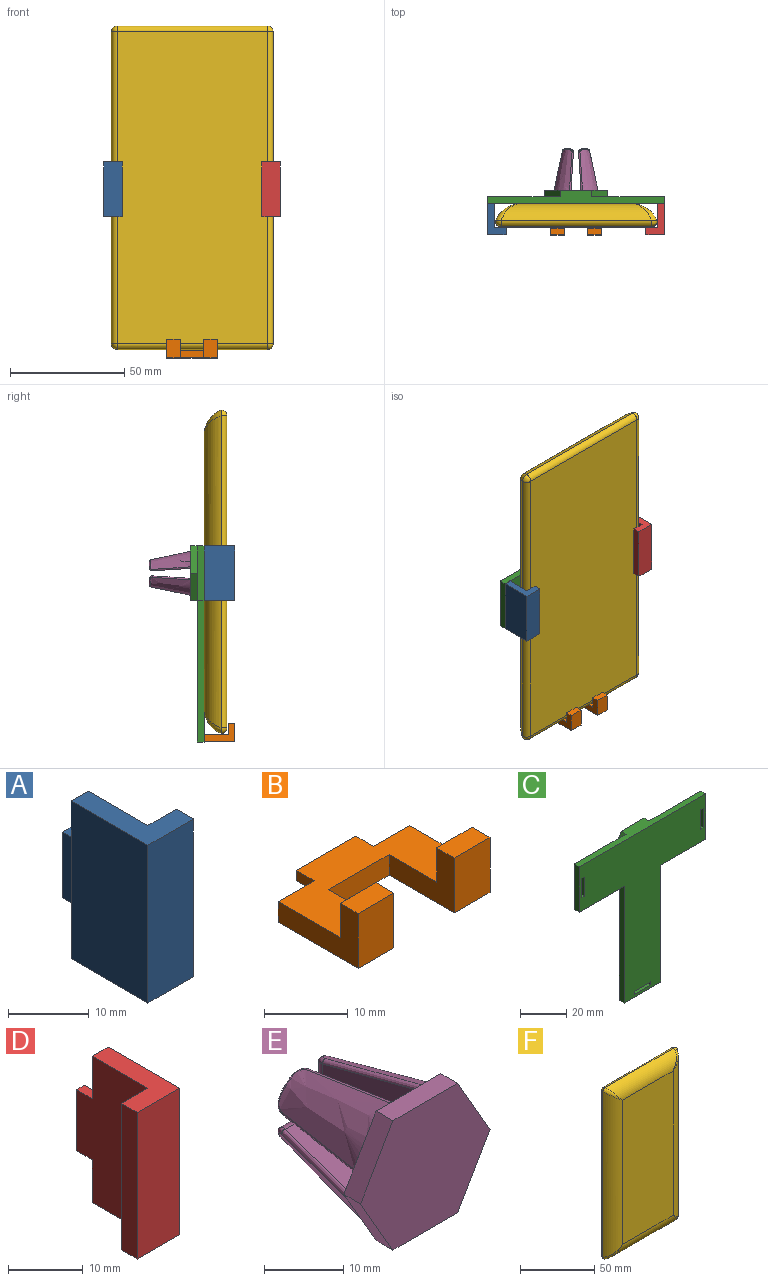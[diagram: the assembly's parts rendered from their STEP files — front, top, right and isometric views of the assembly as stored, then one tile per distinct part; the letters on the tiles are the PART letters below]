
ASSEMBLY  parts=6 mates=5
PART A: 12 faces, bbox 8x16.5x24 mm
  f0: plane 13.5x8mm, normal (0,0,-1), area 55.5mm2, adj f1,f4,f5,f6,f7,f11
  f1: plane 24x13.5mm, normal (1,0,0), area 282mm2, adj f0,f2,f3,f7,f8,f10,f11
  f2: plane 13.5x8mm, normal (0,0,1), area 55.5mm2, adj f1,f4,f5,f6,f7,f11
  f3: plane 10x1.5mm, normal (0,1,0), area 15mm2, adj f1,f8,f9,f10
  f4: plane 24x13.5mm, normal (-1,0,0), area 324mm2, adj f0,f2,f6,f11
  f5: plane 24x3mm, normal (1,0,0), area 72mm2, adj f0,f2,f6,f7
  f6: plane 24x8mm, normal (0,-1,0), area 192mm2, adj f0,f2,f4,f5
  f7: plane 24x5mm, normal (0,1,0), area 120mm2, adj f0,f1,f2,f5
  f8: plane 3x1.5mm, normal (0,0,1), area 4.5mm2, adj f1,f3,f9,f11
  f9: plane 10x3mm, normal (-1,0,0), area 30mm2, adj f3,f8,f10,f11
  f10: plane 3x1.5mm, normal (0,0,-1), area 4.5mm2, adj f1,f3,f9,f11
  f11: plane 24x3mm, normal (0,1,0), area 57mm2, adj f0,f1,f2,f4,f8,f9,f10
PART B: 18 faces, bbox 22.2x16.5x8 mm
  f0: plane 10x1.5mm, normal (0,1,0), area 15mm2, adj f1,f2,f3,f4
  f1: plane 22.2x13.5mm, normal (0,0,1), area 181.5mm2, adj f0,f3,f4,f5,f6,f7,f9,f12
  f2: plane 10x3mm, normal (0,0,-1), area 30mm2, adj f0,f3,f4,f5
  f3: plane 3x1.5mm, normal (-1,0,0), area 4.5mm2, adj f0,f1,f2,f5
  f4: plane 3x1.5mm, normal (1,0,0), area 4.5mm2, adj f0,f1,f2,f5
  f5: plane 22.2x3mm, normal (0,1,0), area 51.6mm2, adj f1,f2,f3,f4,f7,f8,f16
  f6: plane 11x8mm, normal (1,0,0), area 48mm2, adj f1,f8,f9,f10,f11,f17
  f7: plane 13.5x8mm, normal (-1,0,0), area 55.5mm2, adj f1,f5,f8,f9,f10,f11
  f8: plane 22.2x13.5mm, normal (0,0,-1), area 187.5mm2, adj f5,f6,f7,f11,f12,f15,f16,f17
  f9: plane 6x5mm, normal (0,1,0), area 30mm2, adj f1,f6,f7,f10
  f10: plane 6x3mm, normal (0,0,1), area 18mm2, adj f6,f7,f9,f11
  f11: plane 8x6mm, normal (0,-1,0), area 48mm2, adj f6,f7,f8,f10
  f12: plane 11x8mm, normal (-1,0,0), area 48mm2, adj f1,f8,f13,f14,f15,f17
  f13: plane 6x5mm, normal (0,1,0), area 30mm2, adj f1,f12,f14,f16
  f14: plane 6x3mm, normal (0,0,1), area 18mm2, adj f12,f13,f15,f16
  f15: plane 8x6mm, normal (0,-1,0), area 48mm2, adj f8,f12,f14,f16
  f16: plane 13.5x8mm, normal (1,0,0), area 55.5mm2, adj f1,f5,f8,f13,f14,f15
  f17: plane 10.2x3mm, normal (0,-1,0), area 30.6mm2, adj f1,f6,f8,f12
PART C: 35 faces, bbox 77.2x6x85.8 mm
  f0: plane 61.75x3mm, normal (-1,0,0), area 185.2mm2, adj f2,f3,f4,f5
  f1: plane 61.75x3mm, normal (1,0,0), area 185.2mm2, adj f2,f3,f4,f9
  f2: plane 22.2x3mm, normal (0,0,-1), area 66.6mm2, adj f0,f1,f3,f4
  f3: plane 85.75x77.2mm, normal (0,1,0), area 2676.3mm2, adj f0,f1,f2,f5,f6,f7,f8,f9
  f4: plane 85.75x77.2mm, normal (0,-1,0), area 3175.2mm2, adj f0,f1,f2,f5,f6,f7,f8,f9
  f5: plane 27.5x3mm, normal (0,0,-1), area 82.5mm2, adj f0,f3,f4,f8
  f6: plane 24x3mm, normal (1,0,0), area 72mm2, adj f3,f4,f7,f9
  f7: plane 77.2x6mm, normal (0,0,1), area 273.2mm2, adj f3,f4,f6,f8,f16,f17,f21
  f8: plane 24x3mm, normal (-1,0,0), area 72mm2, adj f3,f4,f5,f7
  f9: plane 27.5x3mm, normal (0,0,-1), area 82.5mm2, adj f1,f3,f4,f6
  f10: plane 10.1x5.83mm, normal (0.87,0,-0.5), area 35mm2, adj f11,f20,f21,f22
  f11: plane 10.1x5.83mm, normal (0.87,0,0.5), area 35mm2, adj f10,f12,f21,f22
  f12: plane 11.66x3mm, normal (0,0,1), area 35mm2, adj f11,f13,f21,f22
  f13: plane 10.1x5.83mm, normal (-0.87,0,0.5), area 35mm2, adj f12,f14,f21,f22
  f14: plane 10.1x5.83mm, normal (-0.87,0,-0.5), area 35mm2, adj f13,f20,f21,f22
  f15: plane 12x6.93mm, normal (-0.87,0,-0.5), area 41.6mm2, adj f3,f16,f19,f21
  f16: plane 12x6.93mm, normal (-0.87,0,0.5), area 41.6mm2, adj f3,f7,f15,f21
  f17: plane 12x6.93mm, normal (0.87,0,0.5), area 41.6mm2, adj f3,f7,f18,f21
  f18: plane 12x6.93mm, normal (0.87,0,-0.5), area 41.6mm2, adj f3,f17,f19,f21
  f19: plane 13.86x3mm, normal (0,0,-1), area 41.6mm2, adj f3,f15,f18,f21
  f20: plane 11.66x3mm, normal (0,0,-1), area 35mm2, adj f10,f14,f21,f22
  f21: plane 27.71x24mm, normal (0,1,0), area 145.5mm2, adj f7,f10,f11,f12,f13,f14,f15,f16
  f22: plane 23.33x20.2mm, normal (0,1,0), area 353.4mm2, adj f10,f11,f12,f13,f14,f20
  f23: plane 10.1x3mm, normal (1,0,0), area 30.3mm2, adj f3,f4,f24,f25
  f24: plane 3x1.6mm, normal (0,0,-1), area 4.8mm2, adj f3,f4,f23,f26
  f25: plane 3x1.6mm, normal (0,0,1), area 4.8mm2, adj f3,f4,f23,f26
  f26: plane 10.1x3mm, normal (-1,0,0), area 30.3mm2, adj f3,f4,f24,f25
  f27: plane 10.1x3mm, normal (0,0,1), area 30.3mm2, adj f3,f4,f28,f29
  f28: plane 3x1.6mm, normal (1,0,0), area 4.8mm2, adj f3,f4,f27,f30
  f29: plane 3x1.6mm, normal (-1,0,0), area 4.8mm2, adj f3,f4,f27,f30
  f30: plane 10.1x3mm, normal (0,0,-1), area 30.3mm2, adj f3,f4,f28,f29
  f31: plane 10.1x3mm, normal (1,0,0), area 30.3mm2, adj f3,f4,f32,f33
  f32: plane 3x1.6mm, normal (0,0,-1), area 4.8mm2, adj f3,f4,f31,f34
  f33: plane 3x1.6mm, normal (0,0,1), area 4.8mm2, adj f3,f4,f31,f34
  f34: plane 10.1x3mm, normal (-1,0,0), area 30.3mm2, adj f3,f4,f32,f33
PART D: 12 faces, bbox 8x16.5x24 mm
  f0: plane 13.5x8mm, normal (0,0,-1), area 55.5mm2, adj f1,f3,f5,f6,f7,f11
  f1: plane 24x13.5mm, normal (1,0,0), area 324mm2, adj f0,f4,f6,f11
  f2: plane 10x1.5mm, normal (0,1,0), area 15mm2, adj f3,f8,f9,f10
  f3: plane 24x13.5mm, normal (-1,0,0), area 282mm2, adj f0,f2,f4,f7,f8,f10,f11
  f4: plane 13.5x8mm, normal (0,0,1), area 55.5mm2, adj f1,f3,f5,f6,f7,f11
  f5: plane 24x3mm, normal (-1,0,0), area 72mm2, adj f0,f4,f6,f7
  f6: plane 24x8mm, normal (0,-1,0), area 192mm2, adj f0,f1,f4,f5
  f7: plane 24x5mm, normal (0,1,0), area 120mm2, adj f0,f3,f4,f5
  f8: plane 3x1.5mm, normal (0,0,-1), area 4.5mm2, adj f2,f3,f9,f11
  f9: plane 10x3mm, normal (1,0,0), area 30mm2, adj f2,f8,f10,f11
  f10: plane 3x1.5mm, normal (0,0,1), area 4.5mm2, adj f2,f3,f9,f11
  f11: plane 24x3mm, normal (0,1,0), area 57mm2, adj f0,f1,f3,f4,f8,f9,f10
PART E: 60 faces, bbox 23.2x23.4x20.6 mm
  f0: bspline ~17.61x8.12mm, area 143.4mm2, adj f4,f18,f19,f20,f48,f52
  f1: bspline ~17.61x8.12mm, area 143.4mm2, adj f4,f22,f23,f24,f43,f47
  f2: bspline ~17.61x8.12mm, area 143.4mm2, adj f4,f26,f27,f28,f38,f42
  f3: bspline ~17.61x8.12mm, area 143.4mm2, adj f4,f30,f31,f32,f33,f37
  f4: plane 23.15x20.06mm, normal (0,1,0), area 188.5mm2, adj f0,f1,f2,f3,f6,f7,f9,f10
  f5: plane 2.36x2.36mm, normal (0,1,0), area 3.3mm2, adj f31,f34,f36
  f6: plane 16.4x7.48mm, normal (-1,-0.07,0), area 85.4mm2, adj f4,f29,f32,f34
  f7: plane 16.4x7.48mm, normal (0,-0.07,-1), area 85.4mm2, adj f4,f29,f30,f36
  f8: plane 2.36x2.36mm, normal (0,1,0), area 3.3mm2, adj f27,f39,f41
  f9: plane 16.4x7.48mm, normal (1,-0.07,0), area 85.4mm2, adj f4,f25,f28,f39
  f10: plane 16.4x7.48mm, normal (0,-0.07,-1), area 85.4mm2, adj f4,f25,f26,f41
  f11: plane 2.36x2.36mm, normal (0,1,0), area 3.3mm2, adj f23,f44,f46
  f12: plane 16.4x7.48mm, normal (-1,-0.07,0), area 85.4mm2, adj f4,f21,f24,f44
  f13: plane 16.4x7.48mm, normal (0,-0.07,1), area 85.4mm2, adj f4,f21,f22,f46
  f14: plane 2.36x2.36mm, normal (0,1,0), area 3.3mm2, adj f19,f49,f51
  f15: plane 16.4x7.48mm, normal (0,-0.07,1), area 85.4mm2, adj f4,f17,f20,f49
  f16: plane 16.4x7.48mm, normal (1,-0.07,0), area 85.4mm2, adj f4,f17,f18,f51
  f17: cylinder r=0.5mm len=16.41mm, axis (-0.07,-1,-0.07), area 12.9mm2, adj f4,f15,f16,f50
  f18: bspline ~22.72x5.45mm, area 15.7mm2, adj f0,f4,f16,f52
  f19: bspline ~3.89x3.54mm, area 2.4mm2, adj f0,f14,f48,f52
  f20: bspline ~22.72x5.45mm, area 15.7mm2, adj f0,f4,f15,f48
  f21: cylinder r=0.5mm len=16.41mm, axis (0.07,-1,-0.07), area 12.9mm2, adj f4,f12,f13,f45
  f22: bspline ~22.72x5.45mm, area 15.7mm2, adj f1,f4,f13,f47
  f23: bspline ~3.89x3.54mm, area 2.4mm2, adj f1,f11,f43,f47
  f24: bspline ~22.72x5.45mm, area 15.7mm2, adj f1,f4,f12,f43
  f25: cylinder r=0.5mm len=16.41mm, axis (-0.07,-1,0.07), area 12.9mm2, adj f4,f9,f10,f40
  f26: bspline ~22.72x5.45mm, area 15.7mm2, adj f2,f4,f10,f42
  f27: bspline ~3.89x3.54mm, area 2.4mm2, adj f2,f8,f38,f42
  f28: bspline ~22.72x5.45mm, area 15.7mm2, adj f2,f4,f9,f38
  f29: cylinder r=0.5mm len=16.41mm, axis (-0.07,1,-0.07), area 12.9mm2, adj f4,f6,f7,f35
  f30: bspline ~20.18x4.91mm, area 15.7mm2, adj f3,f4,f7,f37
  f31: bspline ~3.62x3.43mm, area 2.4mm2, adj f3,f5,f33,f37
  f32: bspline ~20.18x4.91mm, area 15.7mm2, adj f3,f4,f6,f33
  f33: bspline ~2.03x1.75mm, area 1.9mm2, adj f3,f31,f32,f34
  f34: cylinder r=1.5mm len=4mm, axis (0,0,-1), area 7.8mm2, adj f5,f6,f33,f35
  f35: bspline ~1.76x1.5mm, area 0.9mm2, adj f29,f34,f36
  f36: cylinder r=1.5mm len=4mm, axis (-1,0,0), area 7.8mm2, adj f5,f7,f35,f37
  f37: bspline ~1.99x1.93mm, area 1.9mm2, adj f3,f30,f31,f36
  f38: bspline ~1.99x1.93mm, area 1.9mm2, adj f2,f27,f28,f39
  f39: cylinder r=1.5mm len=4mm, axis (0,0,-1), area 7.8mm2, adj f8,f9,f38,f40
  f40: bspline ~1.76x1.5mm, area 0.9mm2, adj f25,f39,f41
  f41: cylinder r=1.5mm len=4mm, axis (1,0,0), area 7.8mm2, adj f8,f10,f40,f42
  f42: bspline ~2.03x1.75mm, area 1.9mm2, adj f2,f26,f27,f41
  f43: bspline ~1.99x1.93mm, area 1.9mm2, adj f1,f23,f24,f44
  f44: cylinder r=1.5mm len=4mm, axis (0,0,1), area 7.8mm2, adj f11,f12,f43,f45
  f45: bspline ~1.76x1.5mm, area 0.9mm2, adj f21,f44,f46
  f46: cylinder r=1.5mm len=4mm, axis (-1,0,0), area 7.8mm2, adj f11,f13,f45,f47
  f47: bspline ~2.03x1.75mm, area 1.9mm2, adj f1,f22,f23,f46
  f48: bspline ~1.99x1.93mm, area 1.9mm2, adj f0,f19,f20,f49
  f49: cylinder r=1.5mm len=4mm, axis (1,0,0), area 7.8mm2, adj f14,f15,f48,f50
  f50: bspline ~1.76x1.5mm, area 0.9mm2, adj f17,f49,f51
  f51: cylinder r=1.5mm len=4mm, axis (0,0,1), area 7.8mm2, adj f14,f16,f50,f52
  f52: bspline ~2.03x1.75mm, area 1.9mm2, adj f0,f18,f19,f51
  f53: plane 11.55x3mm, normal (0,0,1), area 34.6mm2, adj f4,f54,f58,f59
  f54: plane 10x5.77mm, normal (0.87,0,0.5), area 34.6mm2, adj f4,f53,f55,f59
  f55: plane 10x5.77mm, normal (0.87,0,-0.5), area 34.6mm2, adj f4,f54,f56,f59
  f56: plane 11.55x3mm, normal (0,0,-1), area 34.6mm2, adj f4,f55,f57,f59
  f57: plane 10x5.77mm, normal (-0.87,0,-0.5), area 34.6mm2, adj f4,f56,f58,f59
  f58: plane 10x5.77mm, normal (-0.87,0,0.5), area 34.6mm2, adj f4,f53,f57,f59
  f59: plane 23.09x20mm, normal (0,-1,0), area 346.4mm2, adj f53,f54,f55,f56,f57,f58
PART F: 18 faces, bbox 70.7x10x141.5 mm
  f0: plane 119.25x48.45mm, normal (0,-1,0), area 5777.9mm2, adj f10,f13,f14,f17
  f1: plane 136.5x65.7mm, normal (0,1,0), area 8968.1mm2, adj f3,f4,f7,f8
  f2: sphere r=2.5mm, area 9.8mm2, adj f3,f4,f11
  f3: cylinder r=2.5mm len=65.7mm, axis (-1,0,0), area 258mm2, adj f1,f2,f5,f13
  f4: cylinder r=2.5mm len=136.5mm, axis (0,0,-1), area 536mm2, adj f1,f2,f6,f10
  f5: sphere r=2.5mm, area 13.4mm2, adj f3,f7,f15
  f6: sphere r=2.5mm, area 9.8mm2, adj f4,f8,f12
  f7: cylinder r=2.5mm len=136.5mm, axis (0,0,1), area 536mm2, adj f1,f5,f9,f17
  f8: cylinder r=2.5mm len=65.7mm, axis (1,0,0), area 258mm2, adj f1,f6,f9,f14
  f9: sphere r=2.5mm, area 6.2mm2, adj f7,f8,f16
  f10: cylinder r=12mm len=136.5mm, axis (0,0,-1), area 1820.5mm2, adj f0,f4,f11,f12
  f11: bspline ~11.12x11.12mm, area 22.9mm2, adj f2,f10,f13
  f12: bspline ~11.12x11.12mm, area 22.9mm2, adj f6,f10,f14
  f13: cylinder r=12mm len=65.7mm, axis (1,0,0), area 812.6mm2, adj f0,f3,f11,f15
  f14: cylinder r=12mm len=65.7mm, axis (1,0,0), area 812.6mm2, adj f0,f8,f12,f16
  f15: bspline ~11.12x11.12mm, area 23.1mm2, adj f5,f13,f17
  f16: bspline ~11.12x11.12mm, area 23.1mm2, adj f9,f14,f17
  f17: cylinder r=12mm len=136.5mm, axis (0,0,-1), area 1820.5mm2, adj f0,f7,f15,f16
PLACE A t=(-81.2,-40.39,27.55)mm
PLACE B t=(-94.2,-40.39,40.65)mm
PLACE C t=(-94.2,-40.39,27.55)mm
PLACE D t=(-107.2,-40.39,27.55)mm
PLACE E t=(-94.2,-57.39,27.55)mm
PLACE F rot(axis=(1,0,0),180deg) t=(-232.27,-70.39,-8.84)mm
MATE fastened B.f0 <-> C.f3  axis (0,1,0) through (-94.2,-57.39,-43.1)mm
MATE fastened E.f59 <-> C.f22  axis (0,-1,0) through (-94.2,-57.39,27.55)mm
MATE planar C.f4 <-> F.f0  axis (0,-1,0) through (-94.2,-60.39,9.41)mm
MATE fastened D.f2 <-> C.f3  axis (0,1,0) through (-57.1,-57.39,27.55)mm
MATE fastened A.f3 <-> C.f3  axis (0,1,0) through (-131.3,-57.39,27.55)mm
